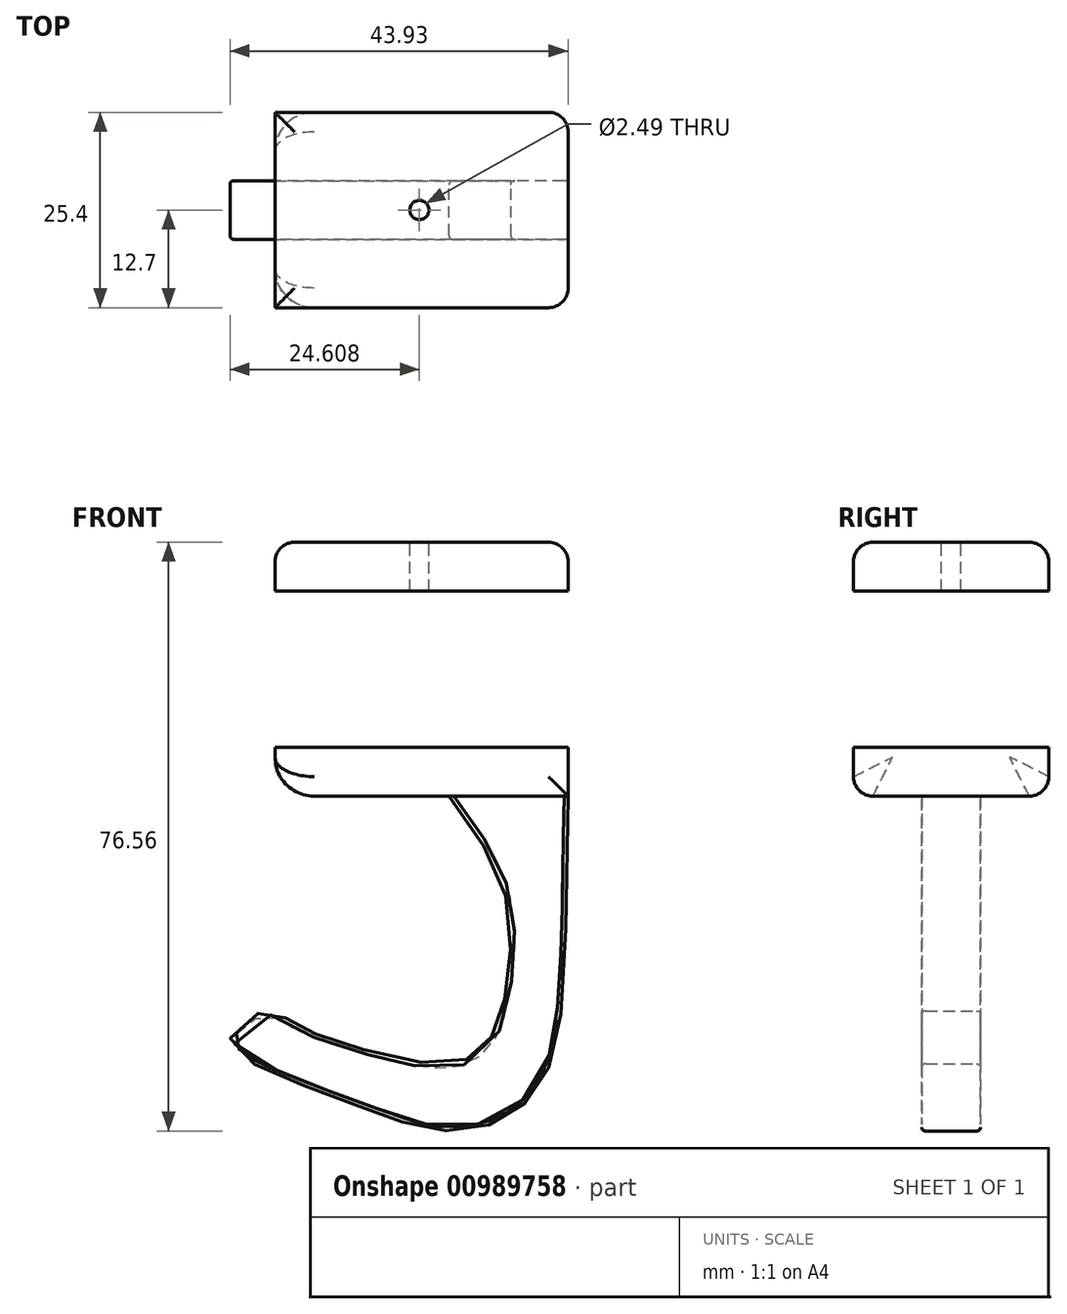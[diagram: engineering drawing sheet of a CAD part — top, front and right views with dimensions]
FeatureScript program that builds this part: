
annotation { "Feature Type Name" : "Feature", "Feature Type Description" : "" }
export const myFeature = defineFeature(function(context is Context, id is Id, definition is map)
    precondition{}
    {
        {
            var Q0;
            Q0=qCreatedBy(makeId("Front.planeOp"),FACE);
            var sketch = newSketch(context, id + "F0", { "sketchPlane" : qUnion([Q0])});
            skLineSegment(sketch, "E0.bottom", {"start": v(-27.65, 40.2) * mm, "end": v(10.45, 40.2) * mm});
            skLineSegment(sketch, "E0.top", {"start": v(-27.65, 33.86) * mm, "end": v(10.45, 33.86) * mm});
            skLineSegment(sketch, "E0.left", {"start": v(-27.65, 40.2) * mm, "end": v(-27.65, 33.86) * mm});
            skLineSegment(sketch, "E0.right", {"start": v(10.45, 40.2) * mm, "end": v(10.45, 33.86) * mm});
            skLineSegment(sketch, "E1.bottom", {"start": v(10.45, 33.86) * mm, "end": v(4.1, 33.86) * mm});
            skLineSegment(sketch, "E1.top", {"start": v(10.45, 13.54) * mm, "end": v(4.1, 13.54) * mm});
            skLineSegment(sketch, "E1.left", {"start": v(10.45, 33.86) * mm, "end": v(10.45, 13.54) * mm});
            skLineSegment(sketch, "E1.right", {"start": v(4.1, 33.86) * mm, "end": v(4.1, 13.54) * mm});
            skLineSegment(sketch, "E2.bottom", {"start": v(10.45, 13.54) * mm, "end": v(-27.65, 13.54) * mm});
            skLineSegment(sketch, "E2.top", {"start": v(10.45, 7.19) * mm, "end": v(-27.65, 7.19) * mm});
            skLineSegment(sketch, "E2.left", {"start": v(10.45, 13.54) * mm, "end": v(10.45, 7.19) * mm});
            skLineSegment(sketch, "E2.right", {"start": v(-27.65, 13.54) * mm, "end": v(-27.65, 7.19) * mm});
            skFitSpline(sketch, "E3", {"points": [v(10.45, 7.19) * mm, v(7.68, -28.72) * mm, v(2.37, -34.6) * mm, v(-5.78, -36.3) * mm, v(-15.26, -33.65) * mm, v(-27.65, -28.91) * mm, v(-33.46, -24.36) * mm, v(-28.72, -20.75) * mm, v(-25.7, -22.09) * mm, v(-18.86, -24.93) * mm, v(-5.02, -27.59) * mm, v(0, -24.93) * mm, v(2.37, -18.3) * mm, v(2.37, -5.78) * mm, v(-5.02, 7.19) * mm], "startDerivative": vector(-9.56, -483.4) * mm, "endDerivative": vector(-116.66, 157.88) * mm});
            skSolve(sketch);
        }
        {
            var Q0;
            {var subQ4=sQuery(id+"F0.wireOp",EDGE,"E2.left");Q0=makeQuery(id+"F0.imprint","IMPRINT",FACE,{"disambiguationData":[TD([[makeQuery(id+"F0.imprint","IMPRINT",EDGE,{"derivedFrom":subQ4}),-1.0]])]});}
            var Q1;
            Q1=makeQuery(id+"F0.imprint","IMPRINT",FACE,{"disambiguationData":[TD([[makeQuery(id+"F0.imprint","IMPRINT",EDGE,{"derivedFrom":sQuery(id+"F0.wireOp",EDGE,"E1.bottom")}),1.0]])]});
            var Q2;
            Q2=makeQuery(id+"F0.imprint","IMPRINT",FACE,{"disambiguationData":[TD([[makeQuery(id+"F0.imprint","IMPRINT",EDGE,{"derivedFrom":sQuery(id+"F0.wireOp",EDGE,"E0.bottom")}),-1.0]])]});
            extrude(context, id + "F1", {"entities" : qUnion([Q0, Q1, Q2]), "endBound" : BoundingType.SYMMETRIC, "depth" : 25.4 * mm, "offsetDistance" : 25.4 * mm});
        }
        {
            var Q0;
            {var subQ0=sQuery(id+"F0.wireOp",EDGE,"E3");Q0=makeQuery(id+"F0.imprint","IMPRINT",FACE,{"disambiguationData":[TD([[makeQuery(id+"F0.imprint","IMPRINT",EDGE,{"derivedFrom":subQ0}),-1.0]])]});}
            extrude(context, id + "F2", {"entities" : qUnion([Q0]), "operationType" : NewBodyOperationType.ADD, "endBound" : BoundingType.SYMMETRIC, "depth" : 7.62 * mm, "offsetDistance" : 25.4 * mm});
        }
        {
            var Q0;
            Q0=makeQuery(id+"F1.opExtrude","SWEPT_EDGE",EDGE,{"disambiguationData":[OSD([sQuery(id+"F0.wireOp",EDGE,"E0.bottom"),sQuery(id+"F0.wireOp",EDGE,"E0.right")])]});
            var Q1;
            Q1=makeQuery(id+"F1.opExtrude","CAP_EDGE",EDGE,{"disambiguationData":[OSD([sQuery(id+"F0.wireOp",EDGE,"E0.bottom")])],"isStart":false});
            var Q2;
            Q2=makeQuery(id+"F1.opExtrude","CAP_EDGE",EDGE,{"disambiguationData":[OSD([sQuery(id+"F0.wireOp",EDGE,"E0.bottom")])],"isStart":true});
            var Q3;
            Q3=makeQuery(id+"F1.opExtrude","SWEPT_EDGE",EDGE,{"disambiguationData":[OSD([sQuery(id+"F0.wireOp",EDGE,"E0.bottom"),sQuery(id+"F0.wireOp",EDGE,"E0.left")])]});
            var Q4;
            Q4=makeQuery(id+"F1.opExtrude","CAP_EDGE",EDGE,{"disambiguationData":[OSD([sQuery(id+"F0.wireOp",EDGE,"E0.right"),sQuery(id+"F0.wireOp",EDGE,"E1.left"),sQuery(id+"F0.wireOp",EDGE,"E2.left")])],"isStart":false});
            var Q5;
            Q5=makeQuery(id+"F1.opExtrude","CAP_EDGE",EDGE,{"disambiguationData":[OSD([sQuery(id+"F0.wireOp",EDGE,"E0.right"),sQuery(id+"F0.wireOp",EDGE,"E1.left"),sQuery(id+"F0.wireOp",EDGE,"E2.left")])],"isStart":true});
            var Q6;
            Q6=makeQuery(id+"F1.opExtrude","CAP_EDGE",EDGE,{"disambiguationData":[OSD([sQuery(id+"F0.wireOp",EDGE,"E2.top")])],"isStart":true});
            var Q7;
            Q7=makeQuery(id+"F1.opExtrude","CAP_EDGE",EDGE,{"disambiguationData":[OSD([sQuery(id+"F0.wireOp",EDGE,"E2.top")])],"isStart":false});
            fillet(context, id + "F3", {"entities" : qUnion([Q0, Q1, Q2, Q3, Q4, Q5, Q6, Q7]), "radius" : 2.54 * mm, "tangentPropagation" : true, "defaultsChanged" : false, "vertexSettings" : [], "allowEdgeOverflow" : false});
        }
        {
            var Q0;
            Q0=makeQuery(id+"F2.opExtrude","CAP_EDGE",EDGE,{"disambiguationData":[OSD([sQuery(id+"F0.wireOp",EDGE,"E3")])],"isStart":false});
            var Q1;
            Q1=makeQuery(id+"F2.opExtrude","CAP_EDGE",EDGE,{"disambiguationData":[OSD([sQuery(id+"F0.wireOp",EDGE,"E3")])],"isStart":true});
            fillet(context, id + "F4", {"entities" : qUnion([Q0, Q1]), "radius" : 0.5 * mm, "tangentPropagation" : true, "rho" : 0.5, "crossSection" : FilletCrossSection.CONIC, "allowEdgeOverflow" : false});
        }
        {
            var Q0;
            Q0=makeQuery(id+"F1.opExtrude","SWEPT_EDGE",EDGE,{"disambiguationData":[OSD([sQuery(id+"F0.wireOp",EDGE,"E2.top"),sQuery(id+"F0.wireOp",EDGE,"E2.right")])]});
            fillet(context, id + "F5", {"entities" : qUnion([Q0]), "radius" : 5.08 * mm, "tangentPropagation" : true, "allowEdgeOverflow" : false});
        }
        {
            var Q0;
            Q0=makeQuery(id+"F1.opExtrude","SWEPT_FACE",FACE,{"disambiguationData":[OSD([sQuery(id+"F0.wireOp",EDGE,"E0.bottom")])]});
            var sketch = newSketch(context, id + "F6", { "sketchPlane" : qUnion([Q0])});
            skCircle(sketch, "E4", {"center": v(-8.87, 0) * mm, "radius": 1.24 * mm});
            skSolve(sketch);
        }
        {
            var Q0;
            Q0=sQuery(id+"F6.wireOp",VERTEX,"E4.center");
            var Q1;
            Q1=makeQuery(id+"F1.opExtrude","SWEPT_BODY",BODY,{"disambiguationData":[OSD([sQuery(id+"F0.wireOp",EDGE,"E0.bottom"),sQuery(id+"F0.wireOp",EDGE,"E0.top"),sQuery(id+"F0.wireOp",EDGE,"E0.left"),sQuery(id+"F0.wireOp",EDGE,"E0.right"),sQuery(id+"F0.wireOp",EDGE,"E1.left"),sQuery(id+"F0.wireOp",EDGE,"E1.right"),sQuery(id+"F0.wireOp",EDGE,"E2.bottom"),sQuery(id+"F0.wireOp",EDGE,"E2.top"),sQuery(id+"F0.wireOp",EDGE,"E2.left"),sQuery(id+"F0.wireOp",EDGE,"E2.right")])]});
            hole(context, id + "F7", {"style" : HoleStyle.SIMPLE, "endStyle" : HoleEndStyle.BLIND, "holeDiameter" : 2.5 * mm, "majorDiameter" : 6.35 * mm, "holeDepth" : 7.62 * mm, "isTappedThrough" : true, "tappedDepth" : 12.7 * mm, "tapClearance" : 3, "startFromSketch" : true, "locations" : qUnion([Q0]), "scope" : qUnion([Q1])});
        }
    });
